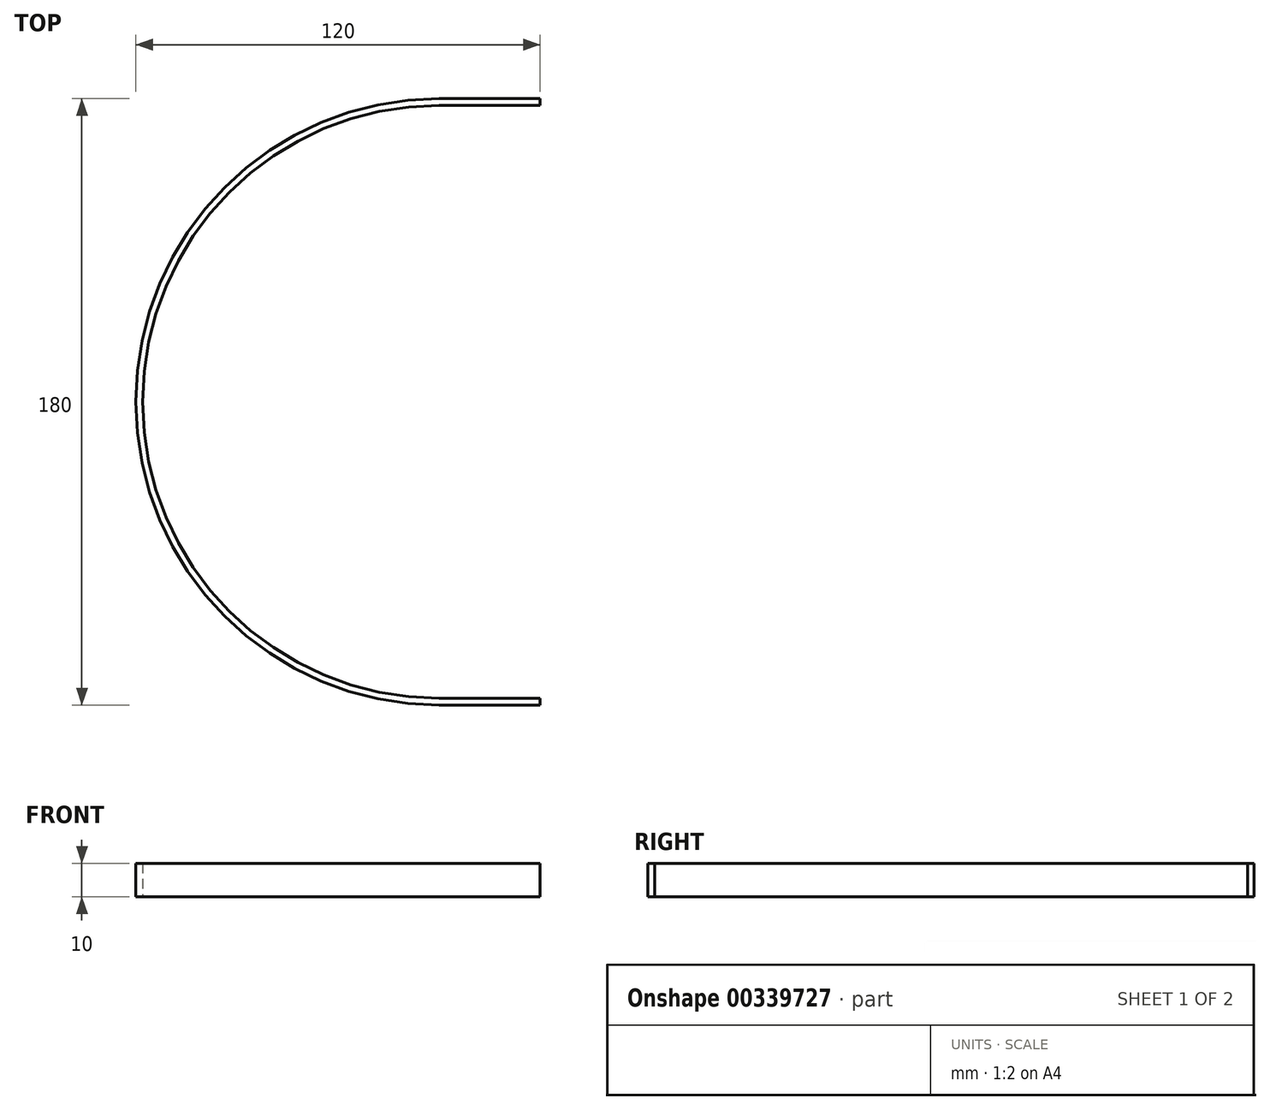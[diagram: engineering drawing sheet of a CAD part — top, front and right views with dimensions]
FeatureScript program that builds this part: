
annotation { "Feature Type Name" : "Feature", "Feature Type Description" : "" }
export const myFeature = defineFeature(function(context is Context, id is Id, definition is map)
    precondition{}
    {
        {
            var Q0;
            Q0=qCreatedBy(makeId("Top.planeOp"),FACE);
            var sketch = newSketch(context, id + "F0", { "sketchPlane" : qUnion([Q0])});
            skArc(sketch, "E0", {"start": v(0, 90) * mm, "mid": v(-90, 0) * mm, "end": v(0, -90) * mm});
            skLineSegment(sketch, "E1", {"start": v(0, 90) * mm, "end": v(0, 88) * mm});
            skLineSegment(sketch, "E2", {"start": v(0, -90) * mm, "end": v(0, -88) * mm});
            skArc(sketch, "E3", {"start": v(0, 88) * mm, "mid": v(-88, 0) * mm, "end": v(0, -88) * mm});
            skSolve(sketch);
        }
        {
            var Q0;
            Q0=makeQuery(id+"F0.imprint","IMPRINT",FACE,{"disambiguationData":[TD([[makeQuery(id+"F0.imprint","IMPRINT",EDGE,{"derivedFrom":sQuery(id+"F0.wireOp",EDGE,"E0")}),1.0]])]});
            extrude(context, id + "F1", {"entities" : qUnion([Q0]), "depth" : 10 * mm});
        }
        {
            var Q0;
            Q0=qCreatedBy(makeId("Front.planeOp"),FACE);
            cPlane(context, id + "F2", {"entities" : qUnion([Q0]), "cplaneType" : CPlaneType.OFFSET, "offset" : 90 * mm, "width" : 150 * mm, "height" : 150 * mm});
        }
        {
            var Q0;
            Q0=makeQuery(id+"F1.opExtrude","SWEPT_FACE",FACE,{"disambiguationData":[OSD([sQuery(id+"F0.wireOp",EDGE,"E2")])]});
            extrude(context, id + "F3", {"entities" : qUnion([Q0]), "operationType" : NewBodyOperationType.ADD, "depth" : 30 * mm});
        }
        {
            var Q0;
            Q0=makeQuery(id+"F1.opExtrude","SWEPT_FACE",FACE,{"disambiguationData":[OSD([sQuery(id+"F0.wireOp",EDGE,"E1")])]});
            extrude(context, id + "F4", {"entities" : qUnion([Q0]), "operationType" : NewBodyOperationType.ADD, "depth" : 30 * mm});
        }
    });
